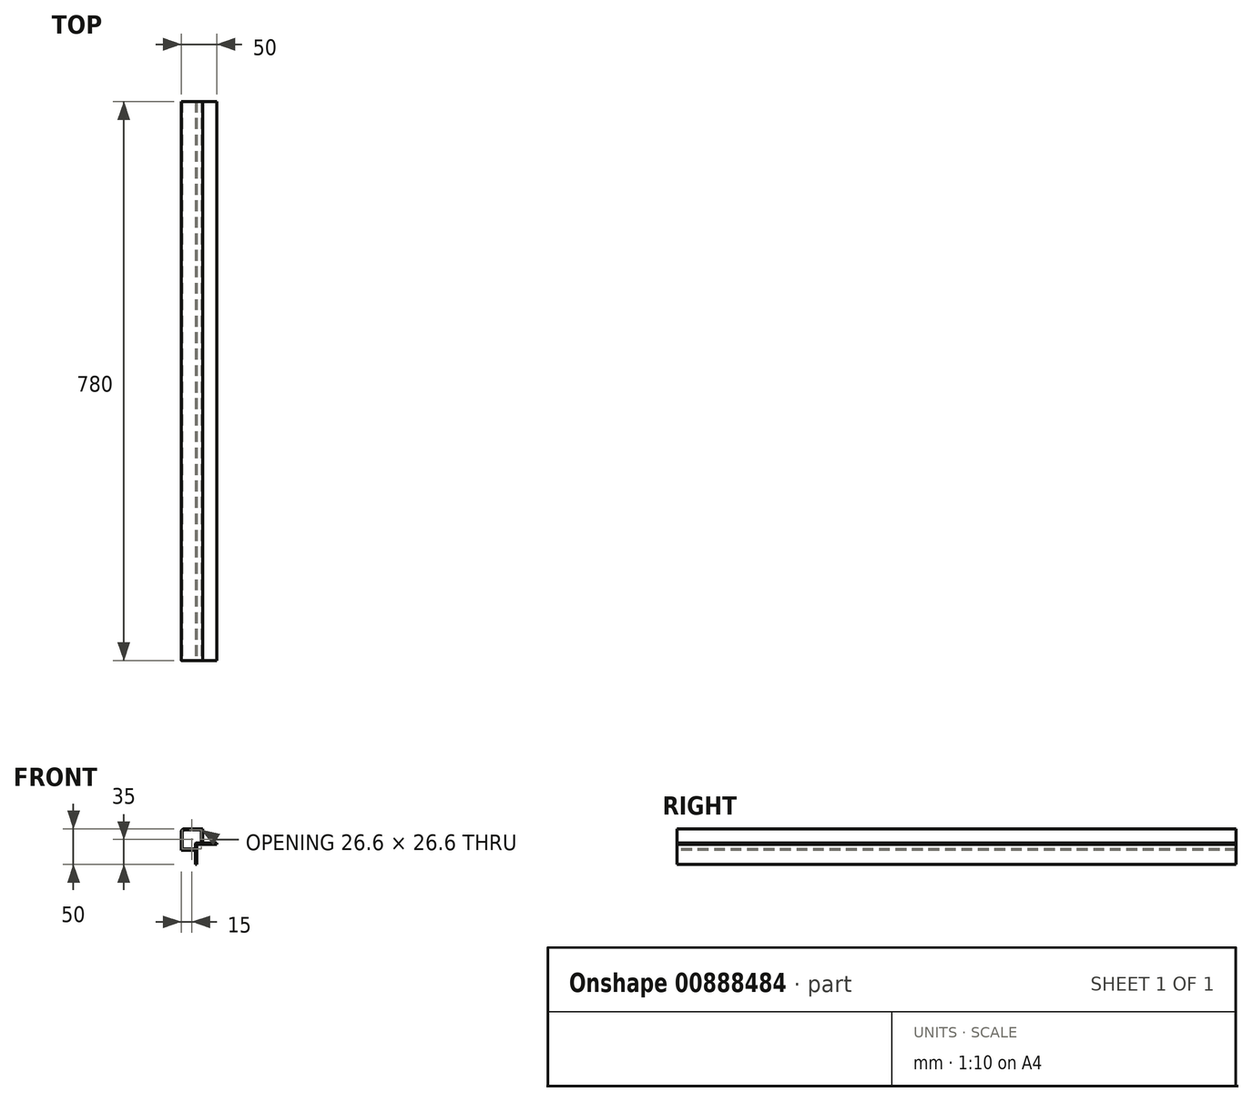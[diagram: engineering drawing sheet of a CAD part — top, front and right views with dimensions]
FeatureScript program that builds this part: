
annotation { "Feature Type Name" : "Feature", "Feature Type Description" : "" }
export const myFeature = defineFeature(function(context is Context, id is Id, definition is map)
    precondition{}
    {
        {
            var Q0;
            Q0=qCreatedBy(makeId("Front.planeOp"),FACE);
            var sketch = newSketch(context, id + "F0", { "sketchPlane" : qUnion([Q0])});
            skLineSegment(sketch, "E0.bottom", {"start": v(-10, 15) * mm, "end": v(15, 15) * mm});
            skLineSegment(sketch, "E0.top", {"start": v(-15, -15) * mm, "end": v(5, -15) * mm});
            skLineSegment(sketch, "E0.left", {"start": v(-15, 10) * mm, "end": v(-15, -15) * mm});
            skLineSegment(sketch, "E0.right", {"start": v(15, 15) * mm, "end": v(15, -5) * mm});
            skPoint(sketch, "E0.middle", {"position": v(0, 0) * mm});
            skLineSegment(sketch, "E1", {"start": v(5, -6) * mm, "end": v(5, -13.3) * mm});
            skLineSegment(sketch, "E2", {"start": v(6, -5) * mm, "end": v(13.3, -5) * mm});
            skPoint(sketch, "E3.orphan", {"position": v(15, -15) * mm});
            skLineSegment(sketch, "E4", {"start": v(35, -5) * mm, "end": v(35, -6.7) * mm});
            skLineSegment(sketch, "E5", {"start": v(35, -6.7) * mm, "end": v(6.7, -6.7) * mm});
            skLineSegment(sketch, "E6", {"start": v(6.7, -6.7) * mm, "end": v(6.7, -35) * mm});
            skLineSegment(sketch, "E7", {"start": v(6.7, -35) * mm, "end": v(5, -35) * mm});
            skLineSegment(sketch, "E8.trimOffspring", {"start": v(15, -5) * mm, "end": v(35, -5) * mm});
            skLineSegment(sketch, "E9.trimOffspring", {"start": v(5, -15) * mm, "end": v(5, -35) * mm});
            skPoint(sketch, "E10.visualSharp", {"position": v(-15, 15) * mm});
            skArc(sketch, "E10.filletArc", {"start": v(-10, 15) * mm, "mid": v(-13.54, 13.54) * mm, "end": v(-15, 10) * mm});
            skLineSegment(sketch, "E11.0", {"start": v(-10, 13.3) * mm, "end": v(13.3, 13.3) * mm});
            skLineSegment(sketch, "E12.0", {"start": v(-13.3, 10) * mm, "end": v(-13.3, -13.3) * mm});
            skArc(sketch, "E12.1", {"start": v(-10, 13.3) * mm, "mid": v(-12.33, 12.33) * mm, "end": v(-13.3, 10) * mm});
            skLineSegment(sketch, "E13.0", {"start": v(13.3, 13.3) * mm, "end": v(13.3, -5) * mm});
            skLineSegment(sketch, "E14.0", {"start": v(-13.3, -13.3) * mm, "end": v(5, -13.3) * mm});
            skPoint(sketch, "E15.visualSharp", {"position": v(5, -5) * mm});
            skArc(sketch, "E15.filletArc", {"start": v(6, -5) * mm, "mid": v(5.3, -5.3) * mm, "end": v(5, -6) * mm});
            skSolve(sketch);
        }
        {
            var Q0;
            Q0 = qSketchRegion(id + "F0", true);
            extrude(context, id + "F1", {"entities" : qUnion([Q0]), "oppositeDirection" : true, "depth" : 780 * mm, "offsetDistance" : 25 * mm});
        }
    });
